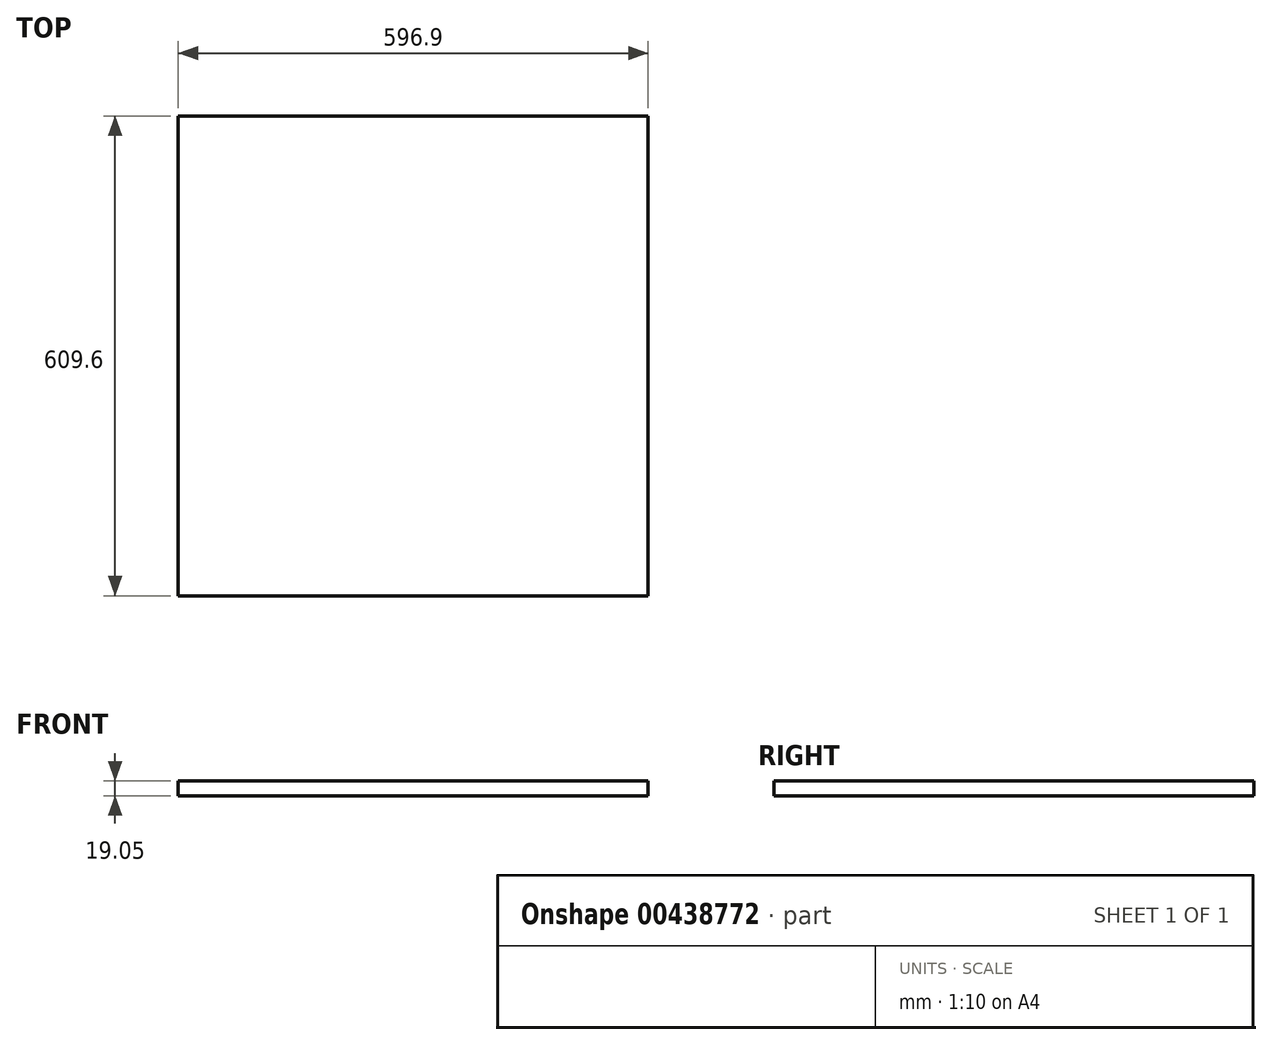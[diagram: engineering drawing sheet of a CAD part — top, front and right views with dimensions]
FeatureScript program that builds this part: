
annotation { "Feature Type Name" : "Feature", "Feature Type Description" : "" }
export const myFeature = defineFeature(function(context is Context, id is Id, definition is map)
    precondition{}
    {
        {
            var Q0;
            Q0=qCreatedBy(makeId("Top.planeOp"),FACE);
            var sketch = newSketch(context, id + "F0", { "sketchPlane" : qUnion([Q0])});
            skLineSegment(sketch, "E0.bottom", {"start": v(298.45, 304.8) * mm, "end": v(-298.45, 304.8) * mm});
            skLineSegment(sketch, "E0.top", {"start": v(298.45, -304.8) * mm, "end": v(-298.45, -304.8) * mm});
            skLineSegment(sketch, "E0.left", {"start": v(298.45, 304.8) * mm, "end": v(298.45, -304.8) * mm});
            skLineSegment(sketch, "E0.right", {"start": v(-298.45, 304.8) * mm, "end": v(-298.45, -304.8) * mm});
            skPoint(sketch, "E0.middle", {"position": v(0, 0) * mm});
            skSolve(sketch);
        }
        {
            var Q0;
            Q0=makeQuery(id+"F0.imprint","IMPRINT",FACE,{"disambiguationData":[TD([[makeQuery(id+"F0.imprint","IMPRINT",EDGE,{"derivedFrom":sQuery(id+"F0.wireOp",EDGE,"E0.bottom")}),1.0]])]});
            extrude(context, id + "F1", {"entities" : qUnion([Q0]), "depth" : 19.05 * mm});
        }
    });
